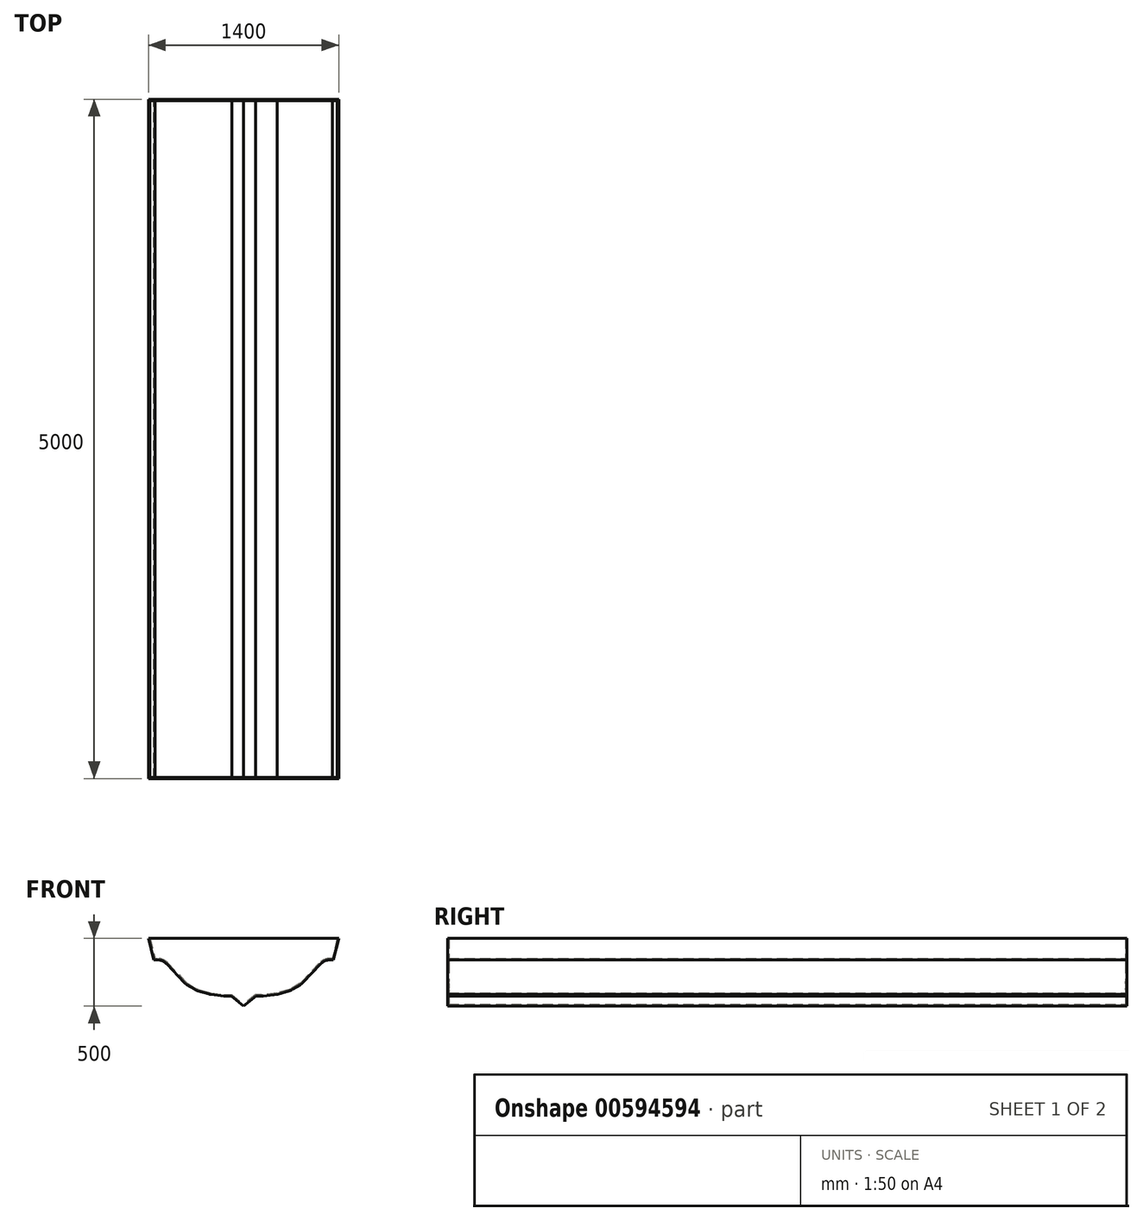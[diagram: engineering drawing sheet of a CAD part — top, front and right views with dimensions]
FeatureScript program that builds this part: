
annotation { "Feature Type Name" : "Feature", "Feature Type Description" : "" }
export const myFeature = defineFeature(function(context is Context, id is Id, definition is map)
    precondition{}
    {
        {
            var Q0;
            Q0=qCreatedBy(makeId("Front.planeOp"),FACE);
            var sketch = newSketch(context, id + "F0", { "sketchPlane" : qUnion([Q0])});
            skLineSegment(sketch, "E0", {"start": v(0, 0) * mm, "end": v(0, 500) * mm});
            skLineSegment(sketch, "E1", {"start": v(0, 500) * mm, "end": v(-700, 500) * mm});
            skLineSegment(sketch, "E2", {"start": v(0, 500) * mm, "end": v(700, 500) * mm});
            skLineSegment(sketch, "E3", {"start": v(-700, 500) * mm, "end": v(-659.97, 341.3) * mm});
            skLineSegment(sketch, "E4", {"start": v(-659.97, 341.3) * mm, "end": v(-636.6, 341.3) * mm});
            skLineSegment(sketch, "E5", {"start": v(-563.38, 309.42) * mm, "end": v(-438.5, 175.17) * mm});
            skLineSegment(sketch, "E6", {"start": v(-417.08, 157.74) * mm, "end": v(-360.72, 123.62) * mm});
            skLineSegment(sketch, "E7", {"start": v(-337.1, 113.2) * mm, "end": v(-256.35, 89.5) * mm});
            skLineSegment(sketch, "E8", {"start": v(-240.69, 86.24) * mm, "end": v(-144.68, 74.14) * mm});
            skLineSegment(sketch, "E9", {"start": v(-132.18, 73.35) * mm, "end": v(-90.3, 73.35) * mm});
            skLineSegment(sketch, "E10", {"start": v(-90.3, 73.35) * mm, "end": v(0, 0) * mm});
            skLineSegment(sketch, "E11.MirrorCS", {"start": v(90.3, 73.35) * mm, "end": v(0, 0) * mm});
            skLineSegment(sketch, "E12.MirrorCS", {"start": v(132.18, 73.35) * mm, "end": v(90.3, 73.35) * mm});
            skLineSegment(sketch, "E13.MirrorCS", {"start": v(248.65, 87.24) * mm, "end": v(144.68, 74.14) * mm});
            skLineSegment(sketch, "E14.MirrorCS", {"start": v(337.1, 113.2) * mm, "end": v(248.65, 87.24) * mm});
            skLineSegment(sketch, "E15.MirrorCS", {"start": v(417.08, 157.74) * mm, "end": v(360.72, 123.62) * mm});
            skLineSegment(sketch, "E16.MirrorCS", {"start": v(563.38, 309.42) * mm, "end": v(438.5, 175.17) * mm});
            skLineSegment(sketch, "E17.MirrorCS", {"start": v(659.97, 341.3) * mm, "end": v(636.6, 341.3) * mm});
            skLineSegment(sketch, "E18.MirrorCS", {"start": v(700, 500) * mm, "end": v(659.97, 341.3) * mm});
            skPoint(sketch, "E19.visualSharp", {"position": v(593.05, 341.3) * mm});
            skArc(sketch, "E19.filletArc", {"start": v(636.6, 341.3) * mm, "mid": v(596.67, 332.99) * mm, "end": v(563.38, 309.42) * mm});
            skPoint(sketch, "E20.visualSharp", {"position": v(-593.05, 341.3) * mm});
            skArc(sketch, "E20.filletArc", {"start": v(-563.38, 309.42) * mm, "mid": v(-596.67, 332.99) * mm, "end": v(-636.6, 341.3) * mm});
            skPoint(sketch, "E21.visualSharp", {"position": v(-349.58, 116.87) * mm});
            skArc(sketch, "E21.filletArc", {"start": v(-360.72, 123.62) * mm, "mid": v(-349.24, 117.65) * mm, "end": v(-337.1, 113.2) * mm});
            skPoint(sketch, "E22.visualSharp", {"position": v(-248.65, 87.24) * mm});
            skArc(sketch, "E22.filletArc", {"start": v(-256.35, 89.5) * mm, "mid": v(-248.58, 87.56) * mm, "end": v(-240.69, 86.24) * mm});
            skPoint(sketch, "E23.visualSharp", {"position": v(-429, 164.96) * mm});
            skArc(sketch, "E23.filletArc", {"start": v(-438.5, 175.17) * mm, "mid": v(-428.4, 165.71) * mm, "end": v(-417.08, 157.74) * mm});
            skPoint(sketch, "E24.visualSharp", {"position": v(-138.46, 73.35) * mm});
            skArc(sketch, "E24.filletArc", {"start": v(-144.68, 74.14) * mm, "mid": v(-138.44, 73.55) * mm, "end": v(-132.18, 73.35) * mm});
            skPoint(sketch, "E25.visualSharp", {"position": v(138.46, 73.35) * mm});
            skArc(sketch, "E25.filletArc", {"start": v(132.18, 73.35) * mm, "mid": v(138.44, 73.55) * mm, "end": v(144.68, 74.14) * mm});
            skPoint(sketch, "E26.visualSharp", {"position": v(349.58, 116.87) * mm});
            skArc(sketch, "E26.filletArc", {"start": v(337.1, 113.2) * mm, "mid": v(349.24, 117.65) * mm, "end": v(360.72, 123.62) * mm});
            skPoint(sketch, "E27.visualSharp", {"position": v(429, 164.96) * mm});
            skArc(sketch, "E27.filletArc", {"start": v(417.08, 157.74) * mm, "mid": v(428.4, 165.71) * mm, "end": v(438.5, 175.17) * mm});
            skSolve(sketch);
        }
        {
            var Q0;
            Q0=makeQuery(id+"F0.imprint","IMPRINT",FACE,{"disambiguationData":[TD([[makeQuery(id+"F0.imprint","IMPRINT",EDGE,{"derivedFrom":sQuery(id+"F0.wireOp",EDGE,"E0")}),-1.0]])]});
            cPlane(context, id + "F1", {"entities" : qUnion([Q0]), "cplaneType" : CPlaneType.OFFSET, "offset" : 1000 * mm, "width" : 150 * mm, "height" : 150 * mm});
        }
        {
            var Q0;
            Q0=makeQuery(id+"F0.imprint","IMPRINT",FACE,{"disambiguationData":[TD([[makeQuery(id+"F0.imprint","IMPRINT",EDGE,{"derivedFrom":sQuery(id+"F0.wireOp",EDGE,"E0")}),1.0]])]});
            var Q1;
            Q1=makeQuery(id+"F0.imprint","IMPRINT",FACE,{"disambiguationData":[TD([[makeQuery(id+"F0.imprint","IMPRINT",EDGE,{"derivedFrom":sQuery(id+"F0.wireOp",EDGE,"E0")}),-1.0]])]});
            extrude(context, id + "F2", {"entities" : qUnion([Q0, Q1]), "depth" : 5000 * mm, "offsetDistance" : 25 * mm});
        }
        {
            var Q0;
            Q0=makeQuery(id+"F2.opExtrude","SWEPT_FACE",FACE,{"disambiguationData":[OSD([sQuery(id+"F0.wireOp",EDGE,"E1"),sQuery(id+"F0.wireOp",EDGE,"E2")])]});
            shell(context, id + "F3", {"entities" : qUnion([Q0]), "thickness" : 10 * mm});
        }
    });
